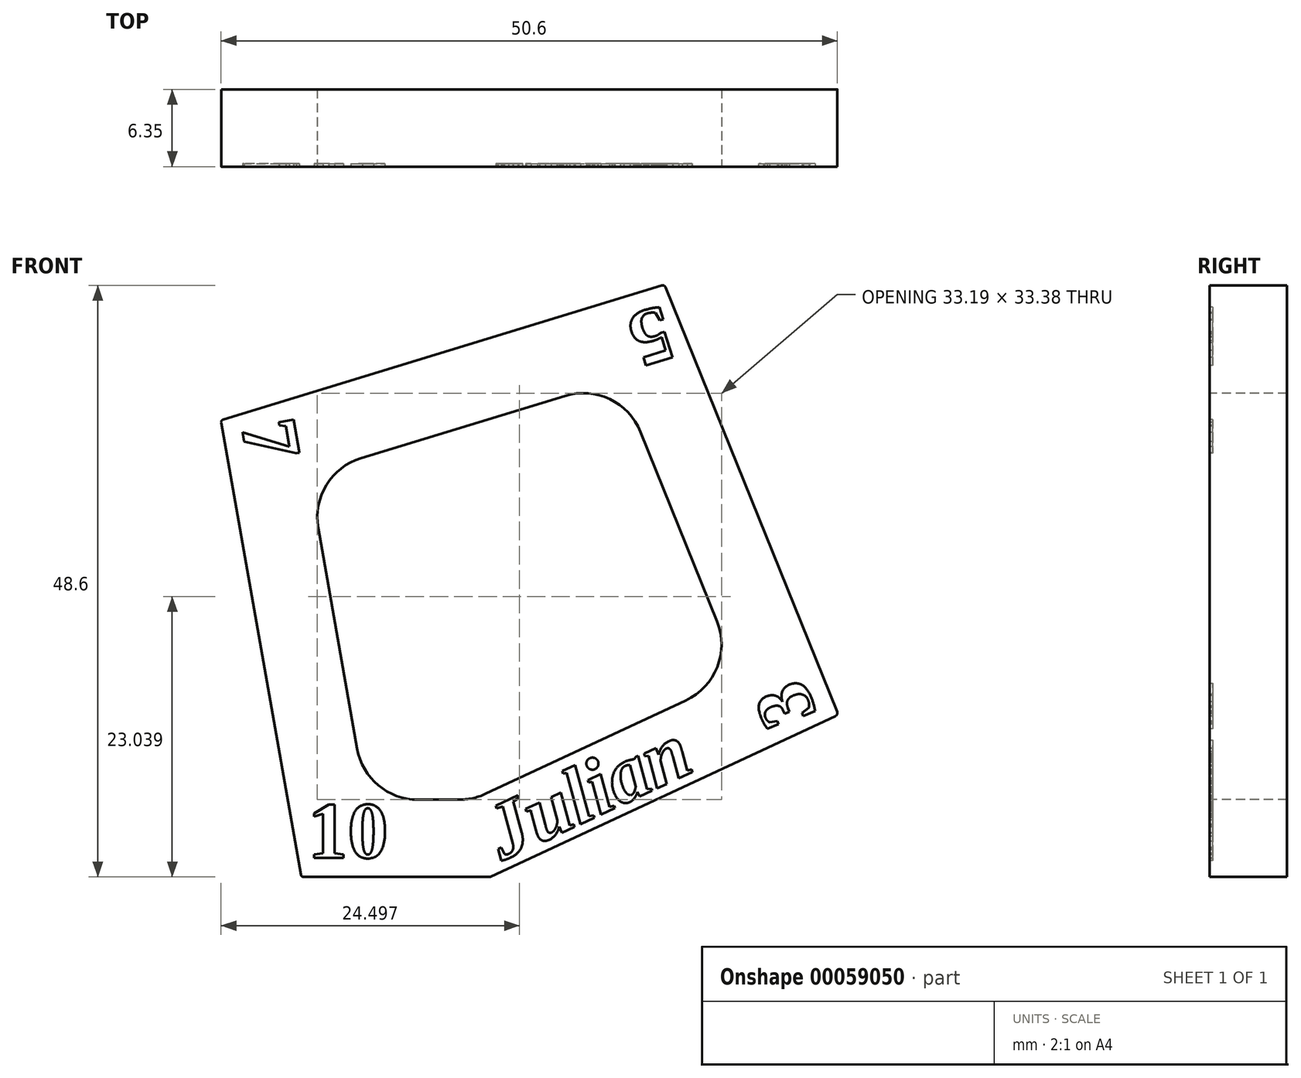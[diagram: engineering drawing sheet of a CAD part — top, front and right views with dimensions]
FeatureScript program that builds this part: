
annotation { "Feature Type Name" : "Feature", "Feature Type Description" : "" }
export const myFeature = defineFeature(function(context is Context, id is Id, definition is map)
    precondition{}
    {
        {
            var Q0;
            Q0=qCreatedBy(makeId("Front.planeOp"),FACE);
            var sketch = newSketch(context, id + "F0", { "sketchPlane" : qUnion([Q0])});
            skLineSegment(sketch, "E0", {"start": v(-24.08, 14.76) * mm, "end": v(-17.47, -22.76) * mm});
            skLineSegment(sketch, "E1", {"start": v(-17.47, -22.76) * mm, "end": v(-1.97, -22.76) * mm});
            skLineSegment(sketch, "E2", {"start": v(-1.97, -22.76) * mm, "end": v(26.62, -9.43) * mm});
            skLineSegment(sketch, "E3", {"start": v(26.62, -9.43) * mm, "end": v(12.35, 25.9) * mm});
            skLineSegment(sketch, "E4", {"start": v(12.35, 25.9) * mm, "end": v(-24.08, 14.76) * mm});
            skCircle(sketch, "E5", {"center": v(0, 0) * mm, "radius": 2.77 * mm, "construction": true});
            skLineSegment(sketch, "E6", {"start": v(-20.83, -3.67) * mm, "end": v(-2.73, -0.48) * mm, "construction": true});
            skLineSegment(sketch, "E7", {"start": v(19.61, 7.92) * mm, "end": v(2.57, 1.04) * mm, "construction": true});
            skLineSegment(sketch, "E8", {"start": v(-6.18, 20.23) * mm, "end": v(-0.8, 2.65) * mm, "construction": true});
            skSolve(sketch);
        }
        {
            var Q0;
            Q0=makeQuery(id+"F0.imprint","IMPRINT",FACE,{"disambiguationData":[TD([[makeQuery(id+"F0.imprint","IMPRINT",EDGE,{"derivedFrom":sQuery(id+"F0.wireOp",EDGE,"E0")}),1.0]])]});
            extrude(context, id + "F1", {"entities" : qUnion([Q0]), "depth" : 6.35 * mm});
        }
        {
            var Q0;
            Q0=makeQuery(id+"F1.opExtrude","CAP_FACE",FACE,{"disambiguationData":[OSD([sQuery(id+"F0.wireOp",EDGE,"E0"),sQuery(id+"F0.wireOp",EDGE,"E1"),sQuery(id+"F0.wireOp",EDGE,"E2"),sQuery(id+"F0.wireOp",EDGE,"E3"),sQuery(id+"F0.wireOp",EDGE,"E4")])],"isStart":false});
            var sketch = newSketch(context, id + "F2", { "sketchPlane" : qUnion([Q0])});
            skLineSegment(sketch, "E9.0", {"start": v(-16.07, 5.9) * mm, "end": v(-12.88, -12.22) * mm});
            skLineSegment(sketch, "E9.1", {"start": v(4.2, 16.76) * mm, "end": v(-12.56, 11.64) * mm});
            skLineSegment(sketch, "E9.2", {"start": v(-7.88, -16.41) * mm, "end": v(-4.5, -16.41) * mm});
            skLineSegment(sketch, "E9.3", {"start": v(-2.36, -15.94) * mm, "end": v(14.11, -8.26) * mm});
            skLineSegment(sketch, "E9.4", {"start": v(16.67, -1.75) * mm, "end": v(10.39, 13.8) * mm});
            skPoint(sketch, "E10.visualSharp", {"position": v(-16.85, 10.33) * mm});
            skArc(sketch, "E10.filletArc", {"start": v(-12.56, 11.64) * mm, "mid": v(-15.4, 9.44) * mm, "end": v(-16.07, 5.9) * mm});
            skPoint(sketch, "E11.visualSharp", {"position": v(-12.14, -16.41) * mm});
            skArc(sketch, "E11.filletArc", {"start": v(-12.88, -12.22) * mm, "mid": v(-11.14, -15.22) * mm, "end": v(-7.88, -16.41) * mm});
            skPoint(sketch, "E12.visualSharp", {"position": v(-3.38, -16.41) * mm});
            skArc(sketch, "E12.filletArc", {"start": v(-4.5, -16.41) * mm, "mid": v(-3.4, -16.3) * mm, "end": v(-2.36, -15.94) * mm});
            skPoint(sketch, "E13.visualSharp", {"position": v(18.48, -6.22) * mm});
            skArc(sketch, "E13.filletArc", {"start": v(14.11, -8.26) * mm, "mid": v(16.7, -5.52) * mm, "end": v(16.67, -1.75) * mm});
            skPoint(sketch, "E14.visualSharp", {"position": v(8.64, 18.12) * mm});
            skArc(sketch, "E14.filletArc", {"start": v(10.39, 13.8) * mm, "mid": v(7.87, 16.49) * mm, "end": v(4.2, 16.76) * mm});
            skSolve(sketch);
        }
        {
            var Q0;
            Q0 = qSketchRegion(id + "F2", true);
            extrude(context, id + "F3", {"entities" : qUnion([Q0]), "operationType" : NewBodyOperationType.REMOVE, "endBound" : BoundingType.THROUGH_ALL, "oppositeDirection" : true, "depth" : 25.4 * mm});
        }
        {
            var Q0;
            Q0=makeQuery(id+"F1.opExtrude","SWEPT_EDGE",EDGE,{"disambiguationData":[OSD([sQuery(id+"F0.wireOp",EDGE,"E0"),sQuery(id+"F0.wireOp",EDGE,"E4")])]});
            var Q1;
            Q1=makeQuery(id+"F1.opExtrude","SWEPT_EDGE",EDGE,{"disambiguationData":[OSD([sQuery(id+"F0.wireOp",EDGE,"E3"),sQuery(id+"F0.wireOp",EDGE,"E4")])]});
            var Q2;
            Q2=makeQuery(id+"F1.opExtrude","SWEPT_EDGE",EDGE,{"disambiguationData":[OSD([sQuery(id+"F0.wireOp",EDGE,"E2"),sQuery(id+"F0.wireOp",EDGE,"E3")])]});
            var Q3;
            Q3=makeQuery(id+"F1.opExtrude","SWEPT_EDGE",EDGE,{"disambiguationData":[OSD([sQuery(id+"F0.wireOp",EDGE,"E1"),sQuery(id+"F0.wireOp",EDGE,"E2")])]});
            var Q4;
            Q4=makeQuery(id+"F1.opExtrude","SWEPT_EDGE",EDGE,{"disambiguationData":[OSD([sQuery(id+"F0.wireOp",EDGE,"E0"),sQuery(id+"F0.wireOp",EDGE,"E1")])]});
            fillet(context, id + "F4", {"entities" : qUnion([Q0, Q1, Q2, Q3, Q4]), "radius" : 0.25 * mm, "tangentPropagation" : true, "allowEdgeOverflow" : false});
        }
        {
            var Q0;
            Q0=makeQuery(id+"F1.opExtrude","CAP_FACE",FACE,{"disambiguationData":[OSD([sQuery(id+"F0.wireOp",EDGE,"E0"),sQuery(id+"F0.wireOp",EDGE,"E1"),sQuery(id+"F0.wireOp",EDGE,"E2"),sQuery(id+"F0.wireOp",EDGE,"E3"),sQuery(id+"F0.wireOp",EDGE,"E4")])],"isStart":false});
            var sketch = newSketch(context, id + "F5", { "sketchPlane" : qUnion([Q0])});
            skText(sketch, "E15", { "text": "10", "fontName": "Tinos-Bold.ttf"});
            skLineSegment(sketch, "E16", {"start": v(-20.97, 6.23) * mm, "end": v(-22.42, 14.44) * mm, "construction": true});
            skLineSegment(sketch, "E17", {"start": v(-22.42, 14.44) * mm, "end": v(-19.4, 14.98) * mm, "construction": true});
            skLineSegment(sketch, "E18", {"start": v(-22.42, 14.44) * mm, "end": v(-22.55, 15.23) * mm, "construction": true});
            skText(sketch, "E19", { "text": "7\n", "fontName": "Tinos-Bold.ttf"});
            skLineSegment(sketch, "E20", {"start": v(-16.95, -21.18) * mm, "end": v(-17.75, -21.18) * mm, "construction": true});
            skLineSegment(sketch, "E21", {"start": v(-17.75, -21.18) * mm, "end": v(-17.75, -21.18) * mm});
            skLineSegment(sketch, "E22", {"start": v(6.87, 22.56) * mm, "end": v(12.2, 24.19) * mm, "construction": true});
            skLineSegment(sketch, "E23", {"start": v(12.2, 24.19) * mm, "end": v(12.95, 24.42) * mm, "construction": true});
            skText(sketch, "E24", { "text": "5", "fontName": "Tinos-Bold.ttf"});
            skLineSegment(sketch, "E25", {"start": v(21.1, 0) * mm, "end": v(24.89, -9.36) * mm, "construction": true});
            skLineSegment(sketch, "E26", {"start": v(24.89, -9.36) * mm, "end": v(25.18, -10.1) * mm, "construction": true});
            skText(sketch, "E27", { "text": "3", "fontName": "Tinos-Bold.ttf"});
            skLineSegment(sketch, "E28", {"start": v(3.06, -19.54) * mm, "end": v(17.36, -12.87) * mm, "construction": true});
            skText(sketch, "E29", { "text": "Julian", "fontName": "Tinos-BoldItalic.ttf"});
            skLineSegment(sketch, "E30", {"start": v(5.02, -13.37) * mm, "end": v(4.69, -12.65) * mm, "construction": true});
            skLineSegment(sketch, "E31", {"start": v(7.03, -17.69) * mm, "end": v(7.37, -18.4) * mm, "construction": true});
            const initialGuessF5  = {"E15": [-0.01695, -0.02118, 1, 0, 0.00476], "E19": [-0.02242, 0.01444, 0.17365, -0.9848, 0.00476], "E24": [0.0122, 0.02419, -0.9563, -0.29237, 0.00476], "E27": [0.02489, -0.00936, -0.3746, 0.92718, 0.00476], "E29": [-0.00101, -0.02144, 0.9063, 0.42262, 0.00476]};
            skSetInitialGuess(sketch, initialGuessF5);
            skSolve(sketch);
        }
        {
            var Q0;
            Q0 = qSketchRegion(id + "F5", true);
            extrude(context, id + "F6", {"entities" : qUnion([Q0]), "operationType" : NewBodyOperationType.REMOVE, "oppositeDirection" : true, "depth" : 0.25 * mm});
        }
    });
